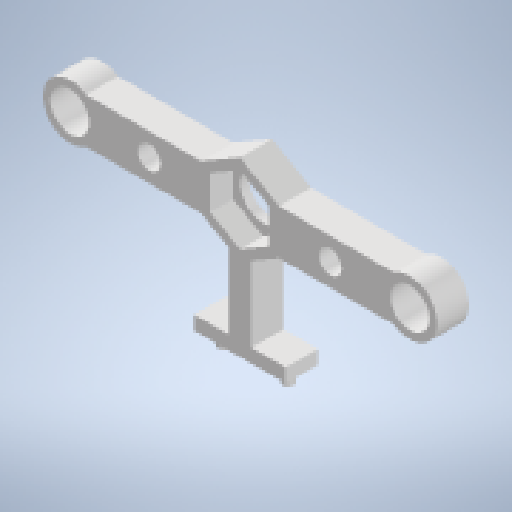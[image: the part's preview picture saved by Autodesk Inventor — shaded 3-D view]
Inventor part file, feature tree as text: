
AUTODESK INVENTOR PART (.ipt)
format: ipt  version: 2023 (Build 270158000, 158)  size: 248,832 bytes
history: native  units: mm
features: extrude x5, reference x5, sketch x3, projected_geometry x3, other x2
ambient origin geometry x8: Origin, YZ Plane, XZ Plane, XY Plane, X Axis, Y Axis, Z Axis, Center Point
bodies: Solid1 (feature_tree)
feature tree (18):
  sketch  "Sketch1"  dims[d0=15.0mm d1=2.0mm]
  extrude  "Extrusion1"  Depth=2.0mm
  extrude  "Extrusion2"  Depth=5.0mm
  extrude  "Extrusion3"  Depth=2.0mm TaperAngle=0.0deg
  extrude  "Extrusion5"  Depth=7.0mm TaperAngle=0.0deg
  extrude  "Extrusion6"  Depth=2.5mm
  reference  "Reference1"
  reference  "Reference2"
  reference  "Reference3"
  reference  "Reference4"
  reference  "Reference5"
  projected_geometry  "Projected Loop4"
  sketch  "Sketch7"  dims[d2=5.0mm d3=5.0mm]
  projected_geometry  "Projected Loop7"
  sketch  "Sketch8"  dims[d4=7.0mm d5=0.0mm d6=2.0mm d7=0.0mm d11=7.0mm d12=0.0mm d13=2.5mm d14=5.0mm d15=20.0mm d16=5.0mm d17=30.0mm d24=20.0mm d25=3.0mm d26=0.0mm d27=3.0mm d28=2.5mm d29=3.0mm d30=0.0mm d31=2.5mm d32=3.0mm d33=0.0mm d8=0.5mm d9=0.872665mm d10=0.5mm d38=0.5mm d39=0.872665mm d40=0.5mm d41=0.872665mm d42=0.872665mm]
  projected_geometry  "Projected Loop8"
  other  "3D_skenner.iam"
  other  "Ogrodje_spodaj_1:1"
